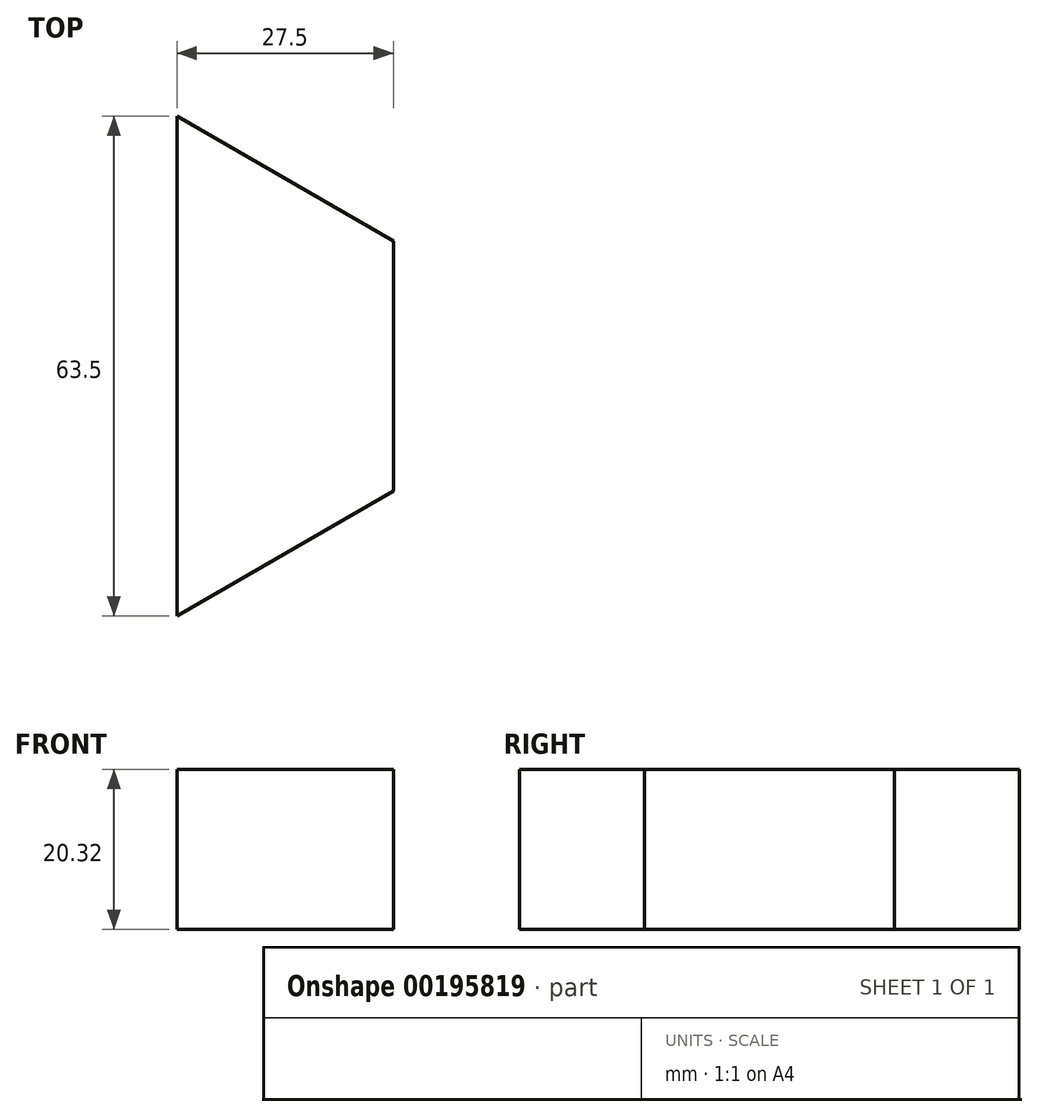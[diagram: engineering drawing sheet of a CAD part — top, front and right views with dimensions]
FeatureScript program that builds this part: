
annotation { "Feature Type Name" : "Feature", "Feature Type Description" : "" }
export const myFeature = defineFeature(function(context is Context, id is Id, definition is map)
    precondition{}
    {
        {
            var Q0;
            Q0=qCreatedBy(makeId("Top.planeOp"),FACE);
            var sketch = newSketch(context, id + "F0", { "sketchPlane" : qUnion([Q0])});
            skLineSegment(sketch, "E0", {"start": v(0, 31.75) * mm, "end": v(0, -31.75) * mm});
            skArc(sketch, "E1", {"start": v(0, -31.75) * mm, "mid": v(31.75, 0) * mm, "end": v(0, 31.75) * mm, "construction": true});
            skPoint(sketch, "E2", {"position": v(31.75, 0) * mm});
            skLineSegment(sketch, "E3", {"start": v(0, 31.75) * mm, "end": v(27.5, 15.88) * mm});
            skLineSegment(sketch, "E4", {"start": v(27.5, 15.88) * mm, "end": v(27.5, -15.88) * mm});
            skLineSegment(sketch, "E5", {"start": v(27.5, -15.88) * mm, "end": v(0, -31.75) * mm});
            skSolve(sketch);
        }
        {
            var Q0;
            Q0=makeQuery(id+"F0.imprint","IMPRINT",FACE,{"disambiguationData":[TD([[makeQuery(id+"F0.imprint","IMPRINT",EDGE,{"derivedFrom":sQuery(id+"F0.wireOp",EDGE,"E0")}),1.0]])]});
            extrude(context, id + "F1", {"entities" : qUnion([Q0]), "depth" : 20.32 * mm});
        }
        {
            var Q0;
            Q0=makeQuery(id+"F1.opExtrude","CAP_FACE",FACE,{"disambiguationData":[OSD([sQuery(id+"F0.wireOp",EDGE,"E0"),sQuery(id+"F0.wireOp",EDGE,"E3"),sQuery(id+"F0.wireOp",EDGE,"E4"),sQuery(id+"F0.wireOp",EDGE,"E5")])],"isStart":false});
            cPlane(context, id + "F2", {"entities" : qUnion([Q0]), "cplaneType" : CPlaneType.OFFSET, "offset" : 30.48 * mm, "width" : 152.4 * mm, "height" : 152.4 * mm});
        }
    });
